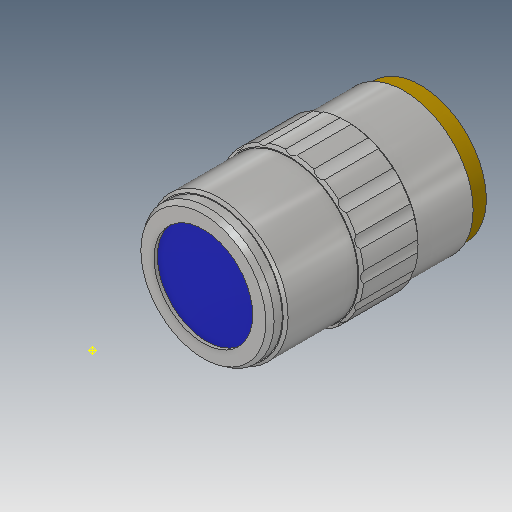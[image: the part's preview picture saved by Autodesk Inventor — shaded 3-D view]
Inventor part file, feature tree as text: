
AUTODESK INVENTOR PART (.ipt)
format: ipt  version: 2021 (Build 250183000, 183)  size: 237,568 bytes
history: native  units: mm
features: extrude x6, sketch x4, chamfer x3, plane x2, other x2, pattern_circular x1
ambient origin geometry x8: Origin, YZ Plane, XZ Plane, XY Plane, X Axis, Y Axis, Z Axis, Center Point
bodies: Solid1 (feature_tree)
feature tree (18):
  sketch  "Sketch1"  dims[d0=39.0mm d1=40.0mm]
  extrude  "Extrusion1"  Depth=40.0mm
  extrude  "Extrusion3"  Depth=4.0mm TaperAngle=0.0deg
  chamfer  "Chamfer2"  Distance=57.0mm
  chamfer  "Chamfer3"  Distance=1.0mm Angle=45.0deg
  extrude  "Extrusion4"  Depth=30.0mm
  extrude  "Extrusion5"  Depth=40.0mm
  plane  "Work Plane1"
  sketch  "Sketch4"  dims[d19=1.0mm d20=0.0mm d21=40.0mm d22=5.0mm d23=0.0mm d24=-22.0mm d25=44.0mm d26=18.0mm d27=0.0mm d28=50.0mm d29=7.0mm d30=18.0mm d31=0.0mm d35=0.75mm d36=1.5mm d37=45.0deg d38=160.0mm d39=360.0deg d41=34.0mm]
  extrude  "Extrusion6"  Depth=5.0mm TaperAngle=0.0deg
  other  "Work Axis Z"
  extrude  "Extrusion7"  [1 undecoded]
  chamfer  "Chamfer4"  Distance=44.0mm
  pattern_circular  "Circular Pattern2"  [2 undecoded]
  other  "Work Point: Focus"
  sketch  "Sketch2"  dims[d2=42.0mm d3=4.0mm d4=0.0mm d7=57.0mm d8=0.0mm d12=1.0mm d13=1.5mm d14=45.0deg]
  sketch  "Sketch3"  dims[d15=0.75mm d16=1.5mm d17=45.0deg d18=30.0mm]
  plane  "Work Plane2"
note: 3 required parameter values undecoded (feature->parameter linkage not recoverable at this tier; creation-order binding heuristic only, values carry confidence <= 0.55)
